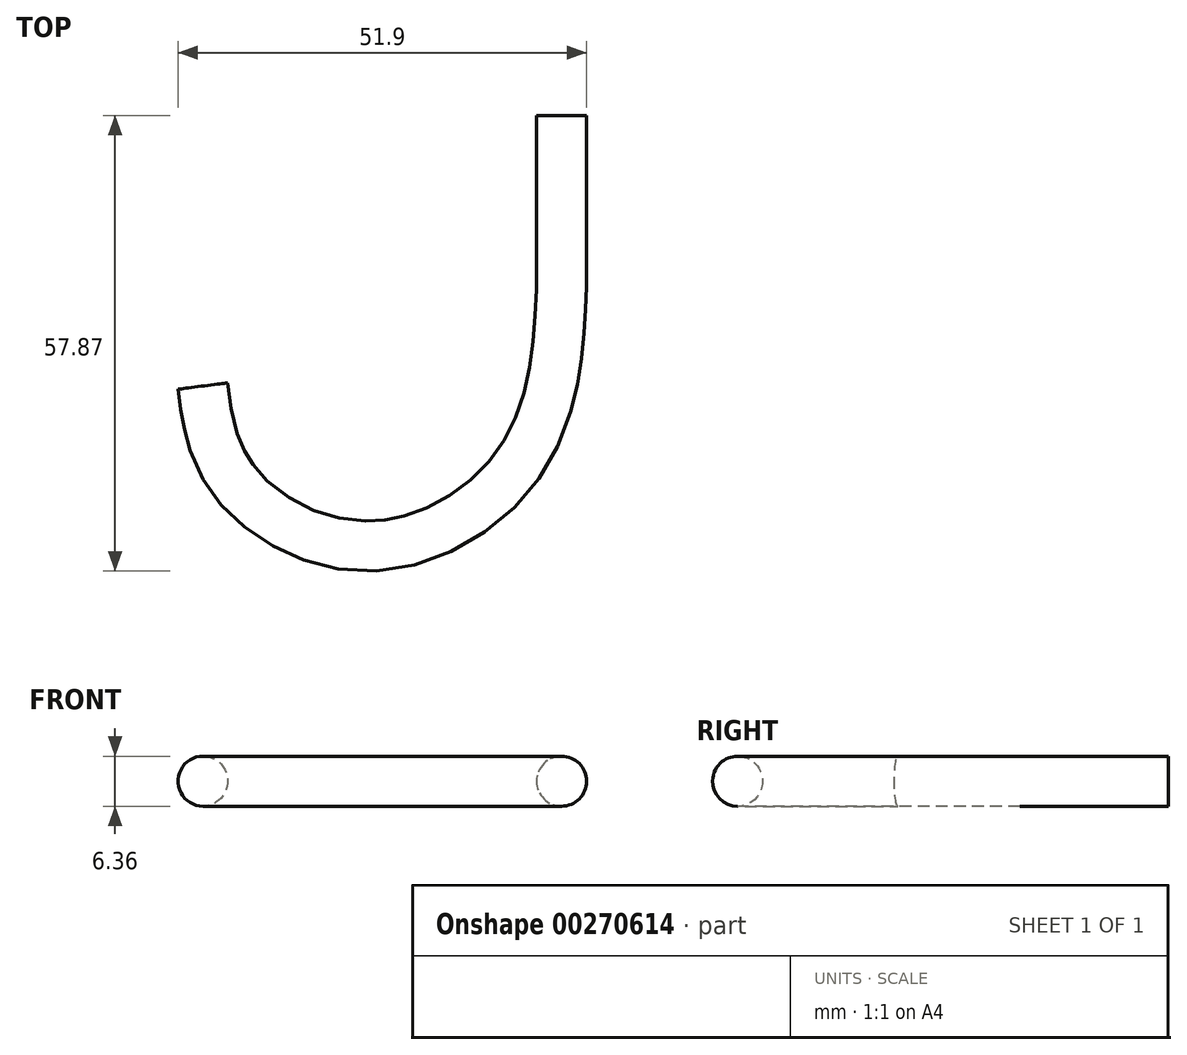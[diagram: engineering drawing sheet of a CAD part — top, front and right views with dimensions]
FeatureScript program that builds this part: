
annotation { "Feature Type Name" : "Feature", "Feature Type Description" : "" }
export const myFeature = defineFeature(function(context is Context, id is Id, definition is map)
    precondition{}
    {
        {
            var Q0;
            Q0=qCreatedBy(makeId("Front.planeOp"),FACE);
            var sketch = newSketch(context, id + "F0", { "sketchPlane" : qUnion([Q0])});
            skCircle(sketch, "E0", {"center": v(0, 0) * mm, "radius": 3.18 * mm});
            skSolve(sketch);
        }
        {
            var Q0;
            Q0=qCreatedBy(makeId("Top.planeOp"),FACE);
            var sketch = newSketch(context, id + "F1", { "sketchPlane" : qUnion([Q0])});
            skLineSegment(sketch, "E1", {"start": v(0, 0) * mm, "end": v(0, -18.81) * mm});
            skFitSpline(sketch, "E2", {"points": [v(0, -18.81) * mm, v(-4.9, -43.43) * mm, v(-24.9, -54.7) * mm, v(-42.25, -45.53) * mm, v(-45.57, -34.35) * mm], "startDerivative": vector(-0.69, -89.8) * mm, "endDerivative": vector(-5.88, 45.25) * mm});
            skSolve(sketch);
        }
        {
            var Q0;
            Q0=makeQuery(id+"F0.imprint","IMPRINT",FACE,{"disambiguationData":[TD([[makeQuery(id+"F0.imprint","IMPRINT",EDGE,{"derivedFrom":sQuery(id+"F0.wireOp",EDGE,"E0")}),1.0]])]});
            var Q1;
            Q1=sQuery(id+"F1.wireOp",EDGE,"E2");
            var Q2;
            Q2=sQuery(id+"F1.wireOp",EDGE,"E1");
            sweep(context, id + "F2", {"profiles" : qUnion([Q0]), "path" : qUnion([Q1, Q2])});
        }
    });
